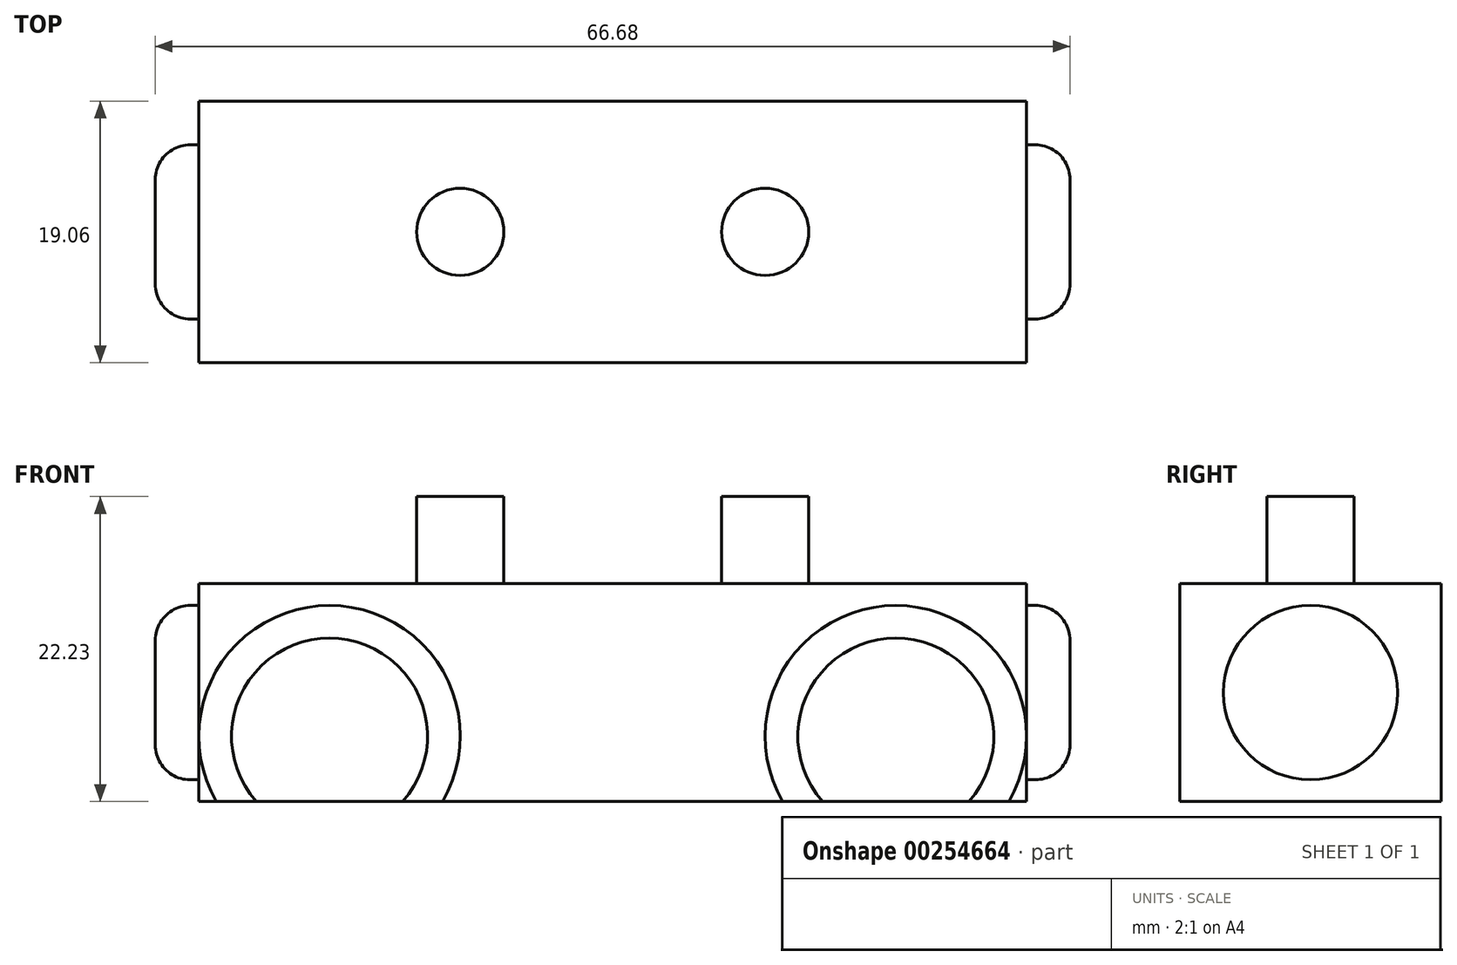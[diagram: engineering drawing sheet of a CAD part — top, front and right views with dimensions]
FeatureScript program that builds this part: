
annotation { "Feature Type Name" : "Feature", "Feature Type Description" : "" }
export const myFeature = defineFeature(function(context is Context, id is Id, definition is map)
    precondition{}
    {
        {
            var Q0;
            Q0=qCreatedBy(makeId("Front.planeOp"),FACE);
            var sketch = newSketch(context, id + "F0", { "sketchPlane" : qUnion([Q0])});
            skLineSegment(sketch, "E0.bottom", {"start": v(30.16, 7.94) * mm, "end": v(-30.16, 7.94) * mm});
            skLineSegment(sketch, "E0.top", {"start": v(30.16, -7.94) * mm, "end": v(-30.16, -7.94) * mm});
            skLineSegment(sketch, "E0.left", {"start": v(30.16, 7.94) * mm, "end": v(30.16, -7.94) * mm});
            skLineSegment(sketch, "E0.right", {"start": v(-30.16, 7.94) * mm, "end": v(-30.16, -7.94) * mm});
            skPoint(sketch, "E0.middle", {"position": v(0, 0) * mm});
            skSolve(sketch);
        }
        {
            var Q0;
            Q0 = qSketchRegion(id + "F0", true);
            extrude(context, id + "F1", {"entities" : qUnion([Q0]), "endBound" : BoundingType.SYMMETRIC, "depth" : 19.05 * mm});
        }
        {
            var Q0;
            Q0=makeQuery(id+"F1.opExtrude","CAP_FACE",FACE,{"disambiguationData":[OSD([sQuery(id+"F0.wireOp",EDGE,"E0.bottom"),sQuery(id+"F0.wireOp",EDGE,"E0.top"),sQuery(id+"F0.wireOp",EDGE,"E0.left"),sQuery(id+"F0.wireOp",EDGE,"E0.right")])],"isStart":false});
            var sketch = newSketch(context, id + "F2", { "sketchPlane" : qUnion([Q0])});
            skLineSegment(sketch, "E1", {"start": v(-30.16, 0) * mm, "end": v(30.16, 0) * mm, "construction": true});
            skCircle(sketch, "E2", {"center": v(20.64, -3.18) * mm, "radius": 9.53 * mm});
            skArc(sketch, "E3", {"start": v(20.64, 1.59) * mm, "mid": v(15.88, -3.17) * mm, "end": v(20.64, -7.94) * mm});
            skLineSegment(sketch, "E4", {"start": v(20.64, -3.18) * mm, "end": v(20.64, 1.59) * mm});
            skLineSegment(sketch, "E5", {"start": v(20.64, 1.59) * mm, "end": v(20.64, -7.94) * mm});
            skLineSegment(sketch, "E6", {"start": v(0, 26.37) * mm, "end": v(0, -14.23) * mm, "construction": true});
            skCircle(sketch, "E7.MirrorC", {"center": v(-20.64, -3.18) * mm, "radius": 9.53 * mm});
            skArc(sketch, "E8.MirrorCS", {"start": v(-20.64, 1.59) * mm, "mid": v(-15.88, -3.18) * mm, "end": v(-20.64, -7.94) * mm});
            skLineSegment(sketch, "E9.MirrorCS", {"start": v(-20.64, 1.59) * mm, "end": v(-20.64, -7.94) * mm});
            skSolve(sketch);
        }
        {
            var Q0;
            {var subQ1=sQuery(id+"F2.wireOp",EDGE,"E3");Q0=makeQuery(id+"F2.imprint","IMPRINT",FACE,{"disambiguationData":[TD([[makeQuery(id+"F2.imprint","IMPRINT",EDGE,{"derivedFrom":subQ1}),-1.0]])]});}
            var Q1;
            {var subQ0=sQuery(id+"F2.wireOp",EDGE,"E3");Q1=makeQuery(id+"F2.imprint","IMPRINT",FACE,{"disambiguationData":[TD([[makeQuery(id+"F2.imprint","IMPRINT",EDGE,{"derivedFrom":subQ0}),1.0]])]});}
            var Q2;
            {var subQ0=sQuery(id+"F2.wireOp",EDGE,"E2");var subQ1=makeQuery(id+"F1.opExtrude","CAP_EDGE",EDGE,{"disambiguationData":[OSD([sQuery(id+"F0.wireOp",EDGE,"E0.top")])],"isStart":false});var subQ2=makeQuery(id+"F2.imprint","INTERSECT",VERTEX,{"disambiguationData":[OD(0.0)],"derivedFrom":[subQ1,subQ0]});Q2=makeQuery(id+"F2.imprint","IMPRINT",FACE,{"disambiguationData":[TD([[makeQuery(id+"F2.imprint","IMPRINT",EDGE,{"disambiguationData":[TD([[subQ2,-1.0]])],"derivedFrom":subQ0}),1.0]])]});}
            extrude(context, id + "F3", {"entities" : qUnion([Q0, Q1, Q2]), "operationType" : NewBodyOperationType.ADD, "depth" : 1 / 203.2 * mm});
        }
        {
            var Q0;
            Q0 = qSketchRegion(id + "F2", true);
            var Q1;
            Q1=sQuery(id+"F2.wireOp",EDGE,"E3");
            var Q2;
            Q2=sQuery(id+"F2.wireOp",EDGE,"E5");
            revolve(context, id + "F4", {"bodyType" : ToolBodyType.SURFACE, "operationType" : NewBodyOperationType.ADD, "entities" : qUnion([Q0]), "surfaceEntities" : qUnion([Q1]), "axis" : qUnion([Q2]), "revolveType" : RevolveType.FULL});
        }
        {
            var Q0;
            Q0=makeQuery(id+"F3.opExtrude","CAP_FACE",FACE,{"disambiguationData":[OSD([sQuery(id+"F2.wireOp",EDGE,"E2")])],"isStart":false});
            var sketch = newSketch(context, id + "F5", { "sketchPlane" : qUnion([Q0])});
            skCircle(sketch, "E10", {"center": v(20.64, -3.18) * mm, "radius": 7.14 * mm});
            skSolve(sketch);
        }
        {
            var Q0;
            Q0 = qSketchRegion(id + "F5", true);
            extrude(context, id + "F6", {"entities" : qUnion([Q0]), "operationType" : NewBodyOperationType.REMOVE, "oppositeDirection" : true, "depth" : 1 / 406.4 * mm});
        }
        {
            var Q0;
            Q0=makeQuery(id+"F4.opRevolve","SWEPT_BODY",BODY,{"disambiguationData":[OSD([sQuery(id+"F2.wireOp",EDGE,"E3")])]});
            var Q1;
            Q1=makeQuery(id+"F1.opExtrude","SWEPT_BODY",BODY,{"disambiguationData":[OSD([sQuery(id+"F0.wireOp",EDGE,"E0.bottom"),sQuery(id+"F0.wireOp",EDGE,"E0.top"),sQuery(id+"F0.wireOp",EDGE,"E0.left"),sQuery(id+"F0.wireOp",EDGE,"E0.right")])]});
            var Q2;
            Q2=qCreatedBy(makeId("Right.planeOp"),FACE);
            mirror(context, id + "F7", {"entities" : qUnion([Q0, Q1]), "mirrorPlane" : qUnion([Q2])});
        }
        {
            var Q0;
            Q0=makeQuery(id+"F1.opExtrude","SWEPT_BODY",BODY,{"disambiguationData":[OSD([sQuery(id+"F0.wireOp",EDGE,"E0.bottom"),sQuery(id+"F0.wireOp",EDGE,"E0.top"),sQuery(id+"F0.wireOp",EDGE,"E0.left"),sQuery(id+"F0.wireOp",EDGE,"E0.right")])]});
            var Q1;
            Q1=makeQuery(id+"F7.opPattern","COPY",BODY,{"derivedFrom":makeQuery(id+"F4.opRevolve","SWEPT_BODY",BODY,{"disambiguationData":[OSD([sQuery(id+"F2.wireOp",EDGE,"E3")])]}),"instanceName":"1"});
            var Q2;
            Q2=makeQuery(id+"F7.opPattern","COPY",BODY,{"derivedFrom":makeQuery(id+"F1.opExtrude","SWEPT_BODY",BODY,{"disambiguationData":[OSD([sQuery(id+"F0.wireOp",EDGE,"E0.bottom"),sQuery(id+"F0.wireOp",EDGE,"E0.top"),sQuery(id+"F0.wireOp",EDGE,"E0.left"),sQuery(id+"F0.wireOp",EDGE,"E0.right")])]}),"instanceName":"1"});
            var Q3;
            Q3=makeQuery(id+"F4.opRevolve","SWEPT_BODY",BODY,{"disambiguationData":[OSD([sQuery(id+"F2.wireOp",EDGE,"E3")])]});
            var Q4;
            Q4=qCreatedBy(makeId("Front.planeOp"),FACE);
            mirror(context, id + "F8", {"entities" : qUnion([Q0, Q1, Q2, Q3]), "mirrorPlane" : qUnion([Q4])});
        }
        {
            var Q0;
            Q0=makeQuery(id+"F1.opExtrude","SWEPT_FACE",FACE,{"disambiguationData":[OSD([sQuery(id+"F0.wireOp",EDGE,"E0.right")])]});
            var sketch = newSketch(context, id + "F9", { "sketchPlane" : qUnion([Q0])});
            skCircle(sketch, "E11", {"center": v(0, 0) * mm, "radius": 6.35 * mm});
            skSolve(sketch);
        }
        {
            var Q0;
            Q0 = qSketchRegion(id + "F9", true);
            extrude(context, id + "F10", {"entities" : qUnion([Q0]), "operationType" : NewBodyOperationType.ADD, "depth" : 3.17 * mm});
        }
        {
            var Q0;
            Q0=makeQuery(id+"F10.opExtrude","CAP_EDGE",EDGE,{"disambiguationData":[OSD([sQuery(id+"F9.wireOp",EDGE,"E11")])],"isStart":false});
            fillet(context, id + "F11", {"entities" : qUnion([Q0]), "radius" : 2.54 * mm, "tangentPropagation" : true, "allowEdgeOverflow" : false});
        }
        {
            var Q0;
            Q0=makeQuery(id+"F10.opExtrude","SWEPT_BODY",BODY,{"disambiguationData":[OSD([sQuery(id+"F9.wireOp",EDGE,"E11")])]});
            var Q1;
            Q1=makeQuery(id+"F1.opExtrude","SWEPT_BODY",BODY,{"disambiguationData":[OSD([sQuery(id+"F0.wireOp",EDGE,"E0.bottom"),sQuery(id+"F0.wireOp",EDGE,"E0.top"),sQuery(id+"F0.wireOp",EDGE,"E0.left"),sQuery(id+"F0.wireOp",EDGE,"E0.right")])]});
            var Q2;
            Q2=qCreatedBy(makeId("Right.planeOp"),FACE);
            mirror(context, id + "F12", {"entities" : qUnion([Q0, Q1]), "mirrorPlane" : qUnion([Q2])});
        }
        {
            var Q0;
            Q0=makeQuery(id+"F1.opExtrude","SWEPT_FACE",FACE,{"disambiguationData":[OSD([sQuery(id+"F0.wireOp",EDGE,"E0.bottom")])]});
            var sketch = newSketch(context, id + "F13", { "sketchPlane" : qUnion([Q0])});
            skCircle(sketch, "E12", {"center": v(-11.11, 0) * mm, "radius": 3.18 * mm});
            skCircle(sketch, "E13.MirrorC", {"center": v(11.11, 0) * mm, "radius": 3.18 * mm});
            skSolve(sketch);
        }
        {
            var Q0;
            Q0 = qSketchRegion(id + "F13", true);
            extrude(context, id + "F14", {"entities" : qUnion([Q0]), "operationType" : NewBodyOperationType.ADD, "depth" : 6.35 * mm});
        }
    });
